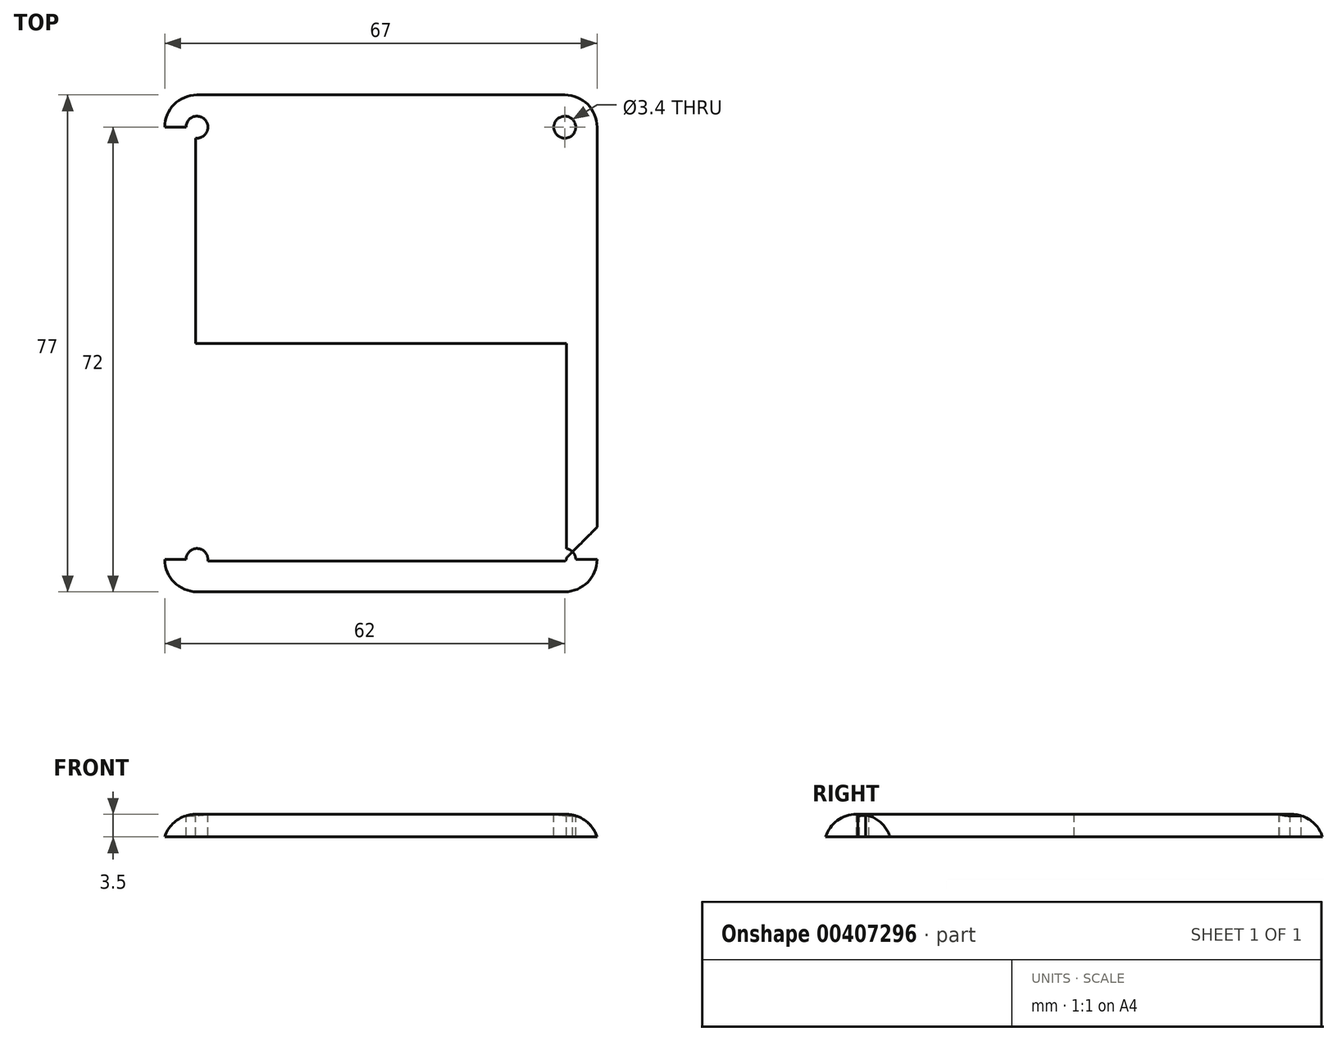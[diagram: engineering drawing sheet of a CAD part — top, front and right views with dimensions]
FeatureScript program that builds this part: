
annotation { "Feature Type Name" : "Feature", "Feature Type Description" : "" }
export const myFeature = defineFeature(function(context is Context, id is Id, definition is map)
    precondition{}
    {
        {
            var Q0;
            Q0=qCreatedBy(makeId("Top.planeOp"),FACE);
            var sketch = newSketch(context, id + "F0", { "sketchPlane" : qUnion([Q0])});
            skLineSegment(sketch, "E0.bottom", {"start": v(0, 0) * mm, "end": v(67, 0) * mm});
            skLineSegment(sketch, "E0.top", {"start": v(0, -77) * mm, "end": v(67, -77) * mm});
            skLineSegment(sketch, "E0.left", {"start": v(0, 0) * mm, "end": v(0, -77) * mm});
            skLineSegment(sketch, "E0.right", {"start": v(67, 0) * mm, "end": v(67, -77) * mm});
            skSolve(sketch);
        }
        {
            var Q0;
            Q0 = qSketchRegion(id + "F0", true);
            extrude(context, id + "F1", {"entities" : qUnion([Q0]), "depth" : 3.5 * mm});
        }
        {
            var Q0;
            Q0=makeQuery(id+"F1.opExtrude","SWEPT_EDGE",EDGE,{"disambiguationData":[OSD([sQuery(id+"F0.wireOp",EDGE,"E0.top"),sQuery(id+"F0.wireOp",EDGE,"E0.right")])]});
            var Q1;
            Q1=makeQuery(id+"F1.opExtrude","SWEPT_EDGE",EDGE,{"disambiguationData":[OSD([sQuery(id+"F0.wireOp",EDGE,"E0.bottom"),sQuery(id+"F0.wireOp",EDGE,"E0.right")])]});
            var Q2;
            Q2=makeQuery(id+"F1.opExtrude","SWEPT_EDGE",EDGE,{"disambiguationData":[OSD([sQuery(id+"F0.wireOp",EDGE,"E0.bottom"),sQuery(id+"F0.wireOp",EDGE,"E0.left")])]});
            var Q3;
            Q3=makeQuery(id+"F1.opExtrude","SWEPT_EDGE",EDGE,{"disambiguationData":[OSD([sQuery(id+"F0.wireOp",EDGE,"E0.top"),sQuery(id+"F0.wireOp",EDGE,"E0.left")])]});
            fillet(context, id + "F2", {"entities" : qUnion([Q0, Q1, Q2, Q3]), "radius" : 5 * mm, "tangentPropagation" : true, "allowEdgeOverflow" : false});
        }
        {
            var Q0;
            Q0=makeQuery(id+"F1.opExtrude","CAP_FACE",FACE,{"disambiguationData":[OSD([sQuery(id+"F0.wireOp",EDGE,"E0.bottom"),sQuery(id+"F0.wireOp",EDGE,"E0.top"),sQuery(id+"F0.wireOp",EDGE,"E0.left"),sQuery(id+"F0.wireOp",EDGE,"E0.right")])],"isStart":false});
            fillet(context, id + "F3", {"entities" : qUnion([Q0]), "radius" : 5 * mm, "tangentPropagation" : true, "allowEdgeOverflow" : false});
        }
        {
            var Q0;
            Q0=makeQuery(id+"F1.opExtrude","CAP_FACE",FACE,{"disambiguationData":[OSD([sQuery(id+"F0.wireOp",EDGE,"E0.bottom"),sQuery(id+"F0.wireOp",EDGE,"E0.top"),sQuery(id+"F0.wireOp",EDGE,"E0.left"),sQuery(id+"F0.wireOp",EDGE,"E0.right")])],"isStart":false});
            var sketch = newSketch(context, id + "F4", { "sketchPlane" : qUnion([Q0])});
            skLineSegment(sketch, "E1", {"start": v(0, 0) * mm, "end": v(5, 0) * mm});
            skLineSegment(sketch, "E2", {"start": v(0, 0) * mm, "end": v(0, -5) * mm});
            skLineSegment(sketch, "E3", {"start": v(0, 0) * mm, "end": v(0, -72) * mm});
            skPoint(sketch, "E3.endSnap0", {"position": v(0, -2.5) * mm});
            skLineSegment(sketch, "E4", {"start": v(0, -72) * mm, "end": v(67, -72) * mm});
            skLineSegment(sketch, "E5", {"start": v(67, -72) * mm, "end": v(67, -67) * mm});
            skLineSegment(sketch, "E6", {"start": v(67, -72) * mm, "end": v(62, -72) * mm});
            skLineSegment(sketch, "E7", {"start": v(0, -5) * mm, "end": v(5, -5) * mm});
            skLineSegment(sketch, "E8", {"start": v(5, -5) * mm, "end": v(5, 0) * mm});
            skCircle(sketch, "E9", {"center": v(5, -5) * mm, "radius": 1.7 * mm});
            skLineSegment(sketch, "E10", {"start": v(62, -72) * mm, "end": v(62, -72) * mm});
            skLineSegment(sketch, "E11", {"start": v(62, -72) * mm, "end": v(67, -67) * mm});
            skCircle(sketch, "E12", {"center": v(62, -72) * mm, "radius": 1.7 * mm});
            skLineSegment(sketch, "E13", {"start": v(4.77, -38.5) * mm, "end": v(62.23, -38.5) * mm});
            skCircle(sketch, "E14.MirrorC", {"center": v(62, -5) * mm, "radius": 1.7 * mm});
            skCircle(sketch, "E15.MirrorC", {"center": v(5, -72) * mm, "radius": 1.7 * mm});
            skSolve(sketch);
        }
        {
            var Q0;
            {var subQ0=sQuery(id+"F4.wireOp",EDGE,"E6");var subQ7=sQuery(id+"F4.wireOp",EDGE,"E12");var subQ8=makeQuery(id+"F4.imprint","INTERSECT",VERTEX,{"derivedFrom":[subQ0,subQ7]});Q0=makeQuery(id+"F4.imprint","IMPRINT",FACE,{"disambiguationData":[TD([[makeQuery(id+"F4.imprint","IMPRINT",EDGE,{"disambiguationData":[TD([[subQ8,-1.0]])],"derivedFrom":subQ7}),1.0]])]});}
            var Q1;
            {var subQ0=sQuery(id+"F4.wireOp",EDGE,"E12");var subQ1=sQuery(id+"F4.wireOp",EDGE,"E11");var subQ2=makeQuery(id+"F4.imprint","INTERSECT",VERTEX,{"derivedFrom":[subQ1,subQ0]});Q1=makeQuery(id+"F4.imprint","IMPRINT",FACE,{"disambiguationData":[TD([[makeQuery(id+"F4.imprint","IMPRINT",EDGE,{"disambiguationData":[TD([[subQ2,1.0]])],"derivedFrom":subQ1}),1.0]])]});}
            var Q2;
            {var subQ1=sQuery(id+"F4.wireOp",EDGE,"E4");var subQ3=sQuery(id+"F4.wireOp",EDGE,"E12");var subQ4=makeQuery(id+"F4.imprint","INTERSECT",VERTEX,{"derivedFrom":[subQ1,subQ3]});Q2=makeQuery(id+"F4.imprint","IMPRINT",FACE,{"disambiguationData":[TD([[makeQuery(id+"F4.imprint","IMPRINT",EDGE,{"disambiguationData":[TD([[subQ4,-1.0]])],"derivedFrom":subQ1}),1.0]])]});}
            var Q3;
            {var subQ0=sQuery(id+"F4.wireOp",EDGE,"E6");var subQ6=sQuery(id+"F4.wireOp",EDGE,"E12");var subQ7=makeQuery(id+"F4.imprint","INTERSECT",VERTEX,{"derivedFrom":[subQ0,subQ6]});Q3=makeQuery(id+"F4.imprint","IMPRINT",FACE,{"disambiguationData":[TD([[makeQuery(id+"F4.imprint","IMPRINT",EDGE,{"disambiguationData":[TD([[subQ7,1.0]])],"derivedFrom":subQ6}),1.0]])]});}
            var Q4;
            {var subQ6=sQuery(id+"F4.wireOp",EDGE,"E4");var subQ8=sQuery(id+"F4.wireOp",EDGE,"E12");var subQ9=makeQuery(id+"F4.imprint","INTERSECT",VERTEX,{"derivedFrom":[subQ6,subQ8]});Q4=makeQuery(id+"F4.imprint","IMPRINT",FACE,{"disambiguationData":[TD([[makeQuery(id+"F4.imprint","IMPRINT",EDGE,{"disambiguationData":[TD([[subQ9,-1.0]])],"derivedFrom":subQ6}),-1.0]])]});}
            var Q5;
            {var subQ0=sQuery(id+"F4.wireOp",EDGE,"E6");var subQ7=sQuery(id+"F4.wireOp",EDGE,"E11");var subQ8=makeQuery(id+"F4.imprint","INTERSECT",VERTEX,{"derivedFrom":[sQuery(id+"F4.wireOp",EDGE,"E4"),subQ0,subQ7]});Q5=makeQuery(id+"F4.imprint","IMPRINT",FACE,{"disambiguationData":[TD([[makeQuery(id+"F4.imprint","IMPRINT",EDGE,{"disambiguationData":[TD([[subQ8,-1.0]])],"derivedFrom":subQ7}),-1.0]])]});}
            var Q6;
            {var subQ0=sQuery(id+"F4.wireOp",EDGE,"E4");var subQ6=sQuery(id+"F4.wireOp",EDGE,"E15.MirrorC");var subQ7=makeQuery(id+"F4.imprint","INTERSECT",VERTEX,{"disambiguationData":[OD(0.0)],"derivedFrom":[subQ0,subQ6]});Q6=makeQuery(id+"F4.imprint","IMPRINT",FACE,{"disambiguationData":[TD([[makeQuery(id+"F4.imprint","IMPRINT",EDGE,{"disambiguationData":[TD([[subQ7,1.0]])],"derivedFrom":subQ6}),-1.0]])]});}
            var Q7;
            {var subQ0=sQuery(id+"F4.wireOp",EDGE,"E4");var subQ7=sQuery(id+"F4.wireOp",EDGE,"E15.MirrorC");var subQ8=makeQuery(id+"F4.imprint","INTERSECT",VERTEX,{"disambiguationData":[OD(0.0)],"derivedFrom":[subQ0,subQ7]});Q7=makeQuery(id+"F4.imprint","IMPRINT",FACE,{"disambiguationData":[TD([[makeQuery(id+"F4.imprint","IMPRINT",EDGE,{"disambiguationData":[TD([[subQ8,-1.0]])],"derivedFrom":subQ7}),-1.0]])]});}
            var Q8;
            {var subQ0=sQuery(id+"F4.wireOp",EDGE,"E4");var subQ7=sQuery(id+"F4.wireOp",EDGE,"E15.MirrorC");var subQ8=makeQuery(id+"F4.imprint","INTERSECT",VERTEX,{"disambiguationData":[OD(1.0)],"derivedFrom":[subQ0,subQ7]});Q8=makeQuery(id+"F4.imprint","IMPRINT",FACE,{"disambiguationData":[TD([[makeQuery(id+"F4.imprint","IMPRINT",EDGE,{"disambiguationData":[TD([[subQ8,1.0]])],"derivedFrom":subQ7}),-1.0]])]});}
            var Q9;
            {var subQ0=sQuery(id+"F4.wireOp",EDGE,"E4");var subQ6=sQuery(id+"F4.wireOp",EDGE,"E15.MirrorC");var subQ7=makeQuery(id+"F4.imprint","INTERSECT",VERTEX,{"disambiguationData":[OD(1.0)],"derivedFrom":[subQ0,subQ6]});Q9=makeQuery(id+"F4.imprint","IMPRINT",FACE,{"disambiguationData":[TD([[makeQuery(id+"F4.imprint","IMPRINT",EDGE,{"disambiguationData":[TD([[subQ7,-1.0]])],"derivedFrom":subQ6}),-1.0]])]});}
            var Q10;
            {var subQ6=sQuery(id+"F4.wireOp",EDGE,"E9");var subQ8=sQuery(id+"F4.wireOp",EDGE,"E8");var subQ9=makeQuery(id+"F4.imprint","INTERSECT",VERTEX,{"derivedFrom":[subQ8,subQ6]});Q10=makeQuery(id+"F4.imprint","IMPRINT",FACE,{"disambiguationData":[TD([[makeQuery(id+"F4.imprint","IMPRINT",EDGE,{"disambiguationData":[TD([[subQ9,-1.0]])],"derivedFrom":subQ6}),1.0]])]});}
            var Q11;
            {var subQ0=sQuery(id+"F4.wireOp",EDGE,"E8");var subQ7=sQuery(id+"F4.wireOp",EDGE,"E9");var subQ8=makeQuery(id+"F4.imprint","INTERSECT",VERTEX,{"derivedFrom":[subQ0,subQ7]});Q11=makeQuery(id+"F4.imprint","IMPRINT",FACE,{"disambiguationData":[TD([[makeQuery(id+"F4.imprint","IMPRINT",EDGE,{"disambiguationData":[TD([[subQ8,1.0]])],"derivedFrom":subQ7}),1.0]])]});}
            var Q12;
            {var subQ1=sQuery(id+"F0.wireOp",EDGE,"E0.left");var subQ2=sQuery(id+"F0.wireOp",EDGE,"E0.bottom");var subQ3=makeQuery(id+"F1.opExtrude","CAP_FACE",FACE,{"disambiguationData":[OSD([subQ2,sQuery(id+"F0.wireOp",EDGE,"E0.top"),subQ1,sQuery(id+"F0.wireOp",EDGE,"E0.right")])],"isStart":false});var subQ4=subQ3;var subQ5=makeQuery(id+"F3.opFillet","BLEND_EDGE",EDGE,{"blendedFrom":[makeQuery(id+"F1.opExtrude","CAP_EDGE",EDGE,{"disambiguationData":[OSD([subQ2])],"isStart":false}),subQ4],"blendedInto":[subQ4]});var subQ8=sQuery(id+"F4.wireOp",EDGE,"E9");var subQ9=makeQuery(id+"F4.imprint","INTERSECT",VERTEX,{"derivedFrom":[subQ5,subQ8]});Q12=makeQuery(id+"F4.imprint","IMPRINT",FACE,{"disambiguationData":[TD([[makeQuery(id+"F4.imprint","IMPRINT",EDGE,{"disambiguationData":[TD([[subQ9,1.0]])],"derivedFrom":subQ8}),1.0]])]});}
            var Q13;
            {var subQ0=sQuery(id+"F4.wireOp",EDGE,"E7");var subQ7=sQuery(id+"F4.wireOp",EDGE,"E9");var subQ8=makeQuery(id+"F4.imprint","INTERSECT",VERTEX,{"derivedFrom":[subQ0,subQ7]});Q13=makeQuery(id+"F4.imprint","IMPRINT",FACE,{"disambiguationData":[TD([[makeQuery(id+"F4.imprint","IMPRINT",EDGE,{"disambiguationData":[TD([[subQ8,-1.0]])],"derivedFrom":subQ7}),1.0]])]});}
            var Q14;
            {var subQ1=sQuery(id+"F0.wireOp",EDGE,"E0.left");var subQ2=sQuery(id+"F0.wireOp",EDGE,"E0.bottom");var subQ3=makeQuery(id+"F1.opExtrude","CAP_FACE",FACE,{"disambiguationData":[OSD([subQ2,sQuery(id+"F0.wireOp",EDGE,"E0.top"),subQ1,sQuery(id+"F0.wireOp",EDGE,"E0.right")])],"isStart":false});var subQ4=subQ3;var subQ5=makeQuery(id+"F3.opFillet","BLEND_EDGE",EDGE,{"blendedFrom":[makeQuery(id+"F2.opFillet","BLEND_EDGE",EDGE,{"blendedFrom":[makeQuery(id+"F1.opExtrude","SWEPT_EDGE",EDGE,{"disambiguationData":[OSD([subQ2,subQ1])]}),subQ3],"blendedInto":[subQ3]}),subQ4],"blendedInto":[subQ4]});Q14=makeQuery(id+"F4.imprint","IMPRINT",FACE,{"disambiguationData":[TD([[makeQuery(id+"F4.imprint","IMPRINT",EDGE,{"derivedFrom":subQ5}),1.0]])]});}
            var Q15;
            {var subQ1=sQuery(id+"F0.wireOp",EDGE,"E0.right");var subQ2=sQuery(id+"F0.wireOp",EDGE,"E0.bottom");var subQ3=makeQuery(id+"F1.opExtrude","CAP_FACE",FACE,{"disambiguationData":[OSD([subQ2,sQuery(id+"F0.wireOp",EDGE,"E0.top"),sQuery(id+"F0.wireOp",EDGE,"E0.left"),subQ1])],"isStart":false});var subQ4=subQ3;var subQ9=makeQuery(id+"F3.opFillet","BLEND_EDGE",EDGE,{"blendedFrom":[makeQuery(id+"F2.opFillet","BLEND_EDGE",EDGE,{"blendedFrom":[makeQuery(id+"F1.opExtrude","SWEPT_EDGE",EDGE,{"disambiguationData":[OSD([subQ2,subQ1])]}),subQ3],"blendedInto":[subQ3]}),subQ4],"blendedInto":[subQ4]});Q15=makeQuery(id+"F4.imprint","IMPRINT",FACE,{"disambiguationData":[TD([[makeQuery(id+"F4.imprint","IMPRINT",EDGE,{"derivedFrom":subQ9}),1.0]])]});}
            var Q16;
            {var subQ1=sQuery(id+"F0.wireOp",EDGE,"E0.right");var subQ2=sQuery(id+"F0.wireOp",EDGE,"E0.bottom");var subQ3=makeQuery(id+"F1.opExtrude","CAP_FACE",FACE,{"disambiguationData":[OSD([subQ2,sQuery(id+"F0.wireOp",EDGE,"E0.top"),sQuery(id+"F0.wireOp",EDGE,"E0.left"),subQ1])],"isStart":false});var subQ4=subQ3;var subQ9=makeQuery(id+"F3.opFillet","BLEND_EDGE",EDGE,{"blendedFrom":[makeQuery(id+"F2.opFillet","BLEND_EDGE",EDGE,{"blendedFrom":[makeQuery(id+"F1.opExtrude","SWEPT_EDGE",EDGE,{"disambiguationData":[OSD([subQ2,subQ1])]}),subQ3],"blendedInto":[subQ3]}),subQ4],"blendedInto":[subQ4]});Q16=makeQuery(id+"F4.imprint","IMPRINT",FACE,{"disambiguationData":[TD([[makeQuery(id+"F4.imprint","IMPRINT",EDGE,{"derivedFrom":subQ9}),-1.0]])]});}
            extrude(context, id + "F5", {"entities" : qUnion([Q0, Q1, Q2, Q3, Q4, Q5, Q6, Q7, Q8, Q9, Q10, Q11, Q12, Q13, Q14, Q15, Q16]), "operationType" : NewBodyOperationType.REMOVE, "oppositeDirection" : true, "depth" : 3.5 * mm});
        }
    });
